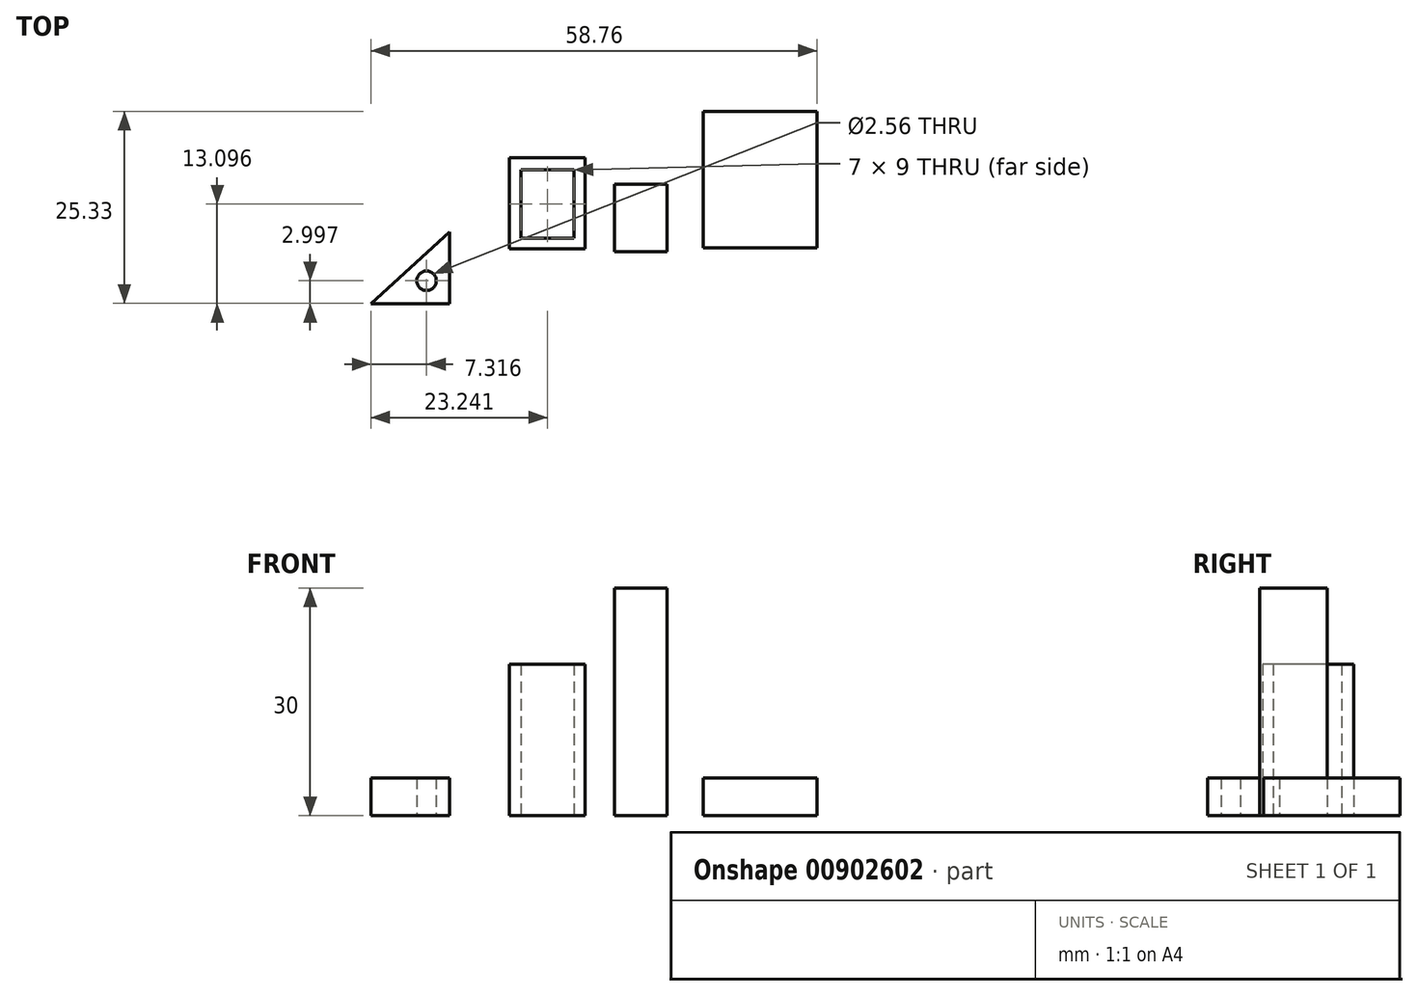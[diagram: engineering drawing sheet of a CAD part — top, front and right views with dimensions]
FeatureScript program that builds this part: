
annotation { "Feature Type Name" : "Feature", "Feature Type Description" : "" }
export const myFeature = defineFeature(function(context is Context, id is Id, definition is map)
    precondition{}
    {
        {
            var Q0;
            Q0=qCreatedBy(makeId("Top.planeOp"),FACE);
            var sketch = newSketch(context, id + "F0", { "sketchPlane" : qUnion([Q0])});
            skLineSegment(sketch, "E0", {"start": v(-29.03, -4.2) * mm, "end": v(-39.38, -13.62) * mm});
            skLineSegment(sketch, "E1", {"start": v(-39.38, -13.62) * mm, "end": v(-29.03, -13.62) * mm});
            skLineSegment(sketch, "E2", {"start": v(-29.03, -4.2) * mm, "end": v(-29.03, -13.62) * mm});
            skPoint(sketch, "E3.center.orphan", {"position": v(-11.7, -10.62) * mm});
            skPoint(sketch, "E4.start.orphan", {"position": v(-14.59, -4.2) * mm});
            skPoint(sketch, "E5.end.orphan", {"position": v(-14.59, -13.62) * mm});
            skPoint(sketch, "E5.start.orphan", {"position": v(-4.24, -13.62) * mm});
            skPoint(sketch, "E6.center.orphan", {"position": v(-32.06, -10.62) * mm});
            skCircle(sketch, "E7", {"center": v(-32.06, -10.62) * mm, "radius": 1.28 * mm});
            skSolve(sketch);
        }
        {
            var Q0;
            Q0=qCreatedBy(makeId("Top.planeOp"),FACE);
            var sketch = newSketch(context, id + "F1", { "sketchPlane" : qUnion([Q0])});
            skLineSegment(sketch, "E8.bottom", {"start": v(-21.17, 5.6) * mm, "end": v(-11.17, 5.6) * mm});
            skLineSegment(sketch, "E8.top", {"start": v(-21.17, -6.4) * mm, "end": v(-11.17, -6.4) * mm});
            skLineSegment(sketch, "E8.left", {"start": v(-21.17, 5.6) * mm, "end": v(-21.17, -6.4) * mm});
            skLineSegment(sketch, "E8.right", {"start": v(-11.17, 5.6) * mm, "end": v(-11.17, -6.4) * mm});
            skLineSegment(sketch, "E9.bottom", {"start": v(-19.64, 3.98) * mm, "end": v(-12.64, 3.98) * mm});
            skLineSegment(sketch, "E9.top", {"start": v(-19.64, -5.02) * mm, "end": v(-12.64, -5.02) * mm});
            skLineSegment(sketch, "E9.left", {"start": v(-19.64, 3.98) * mm, "end": v(-19.64, -5.02) * mm});
            skLineSegment(sketch, "E9.right", {"start": v(-12.64, 3.98) * mm, "end": v(-12.64, -5.02) * mm});
            skSolve(sketch);
        }
        {
            var Q0;
            Q0=qCreatedBy(makeId("Top.planeOp"),FACE);
            var sketch = newSketch(context, id + "F2", { "sketchPlane" : qUnion([Q0])});
            skLineSegment(sketch, "E10.bottom", {"start": v(-7.3, 2.09) * mm, "end": v(-0.4, 2.09) * mm});
            skLineSegment(sketch, "E10.top", {"start": v(-7.3, -6.81) * mm, "end": v(-0.4, -6.81) * mm});
            skLineSegment(sketch, "E10.left", {"start": v(-7.3, 2.09) * mm, "end": v(-7.3, -6.81) * mm});
            skLineSegment(sketch, "E10.right", {"start": v(-0.4, 2.09) * mm, "end": v(-0.4, -6.81) * mm});
            skSolve(sketch);
        }
        {
            var Q0;
            Q0=makeQuery(id+"F0.imprint","IMPRINT",FACE,{"disambiguationData":[TD([[makeQuery(id+"F0.imprint","IMPRINT",EDGE,{"derivedFrom":sQuery(id+"F0.wireOp",EDGE,"E0")}),1.0]])]});
            extrude(context, id + "F3", {"entities" : qUnion([Q0]), "depth" : 5 * mm, "offsetDistance" : 25 * mm});
        }
        {
            var Q0;
            Q0=makeQuery(id+"F1.imprint","IMPRINT",FACE,{"disambiguationData":[TD([[makeQuery(id+"F1.imprint","IMPRINT",EDGE,{"derivedFrom":sQuery(id+"F1.wireOp",EDGE,"E8.bottom")}),-1.0]])]});
            extrude(context, id + "F4", {"entities" : qUnion([Q0]), "depth" : 20 * mm, "offsetDistance" : 25 * mm});
        }
        {
            var Q0;
            Q0=makeQuery(id+"F2.imprint","IMPRINT",FACE,{"disambiguationData":[TD([[makeQuery(id+"F2.imprint","IMPRINT",EDGE,{"derivedFrom":sQuery(id+"F2.wireOp",EDGE,"E10.bottom")}),-1.0]])]});
            extrude(context, id + "F5", {"entities" : qUnion([Q0]), "depth" : 30 * mm, "offsetDistance" : 25 * mm});
        }
        {
            var Q0;
            Q0=qCreatedBy(makeId("Top.planeOp"),FACE);
            var sketch = newSketch(context, id + "F6", { "sketchPlane" : qUnion([Q0])});
            skLineSegment(sketch, "E11.bottom", {"start": v(4.38, 11.71) * mm, "end": v(19.38, 11.71) * mm});
            skLineSegment(sketch, "E11.top", {"start": v(4.38, -6.29) * mm, "end": v(19.38, -6.29) * mm});
            skLineSegment(sketch, "E11.left", {"start": v(4.38, 11.71) * mm, "end": v(4.38, -6.29) * mm});
            skLineSegment(sketch, "E11.right", {"start": v(19.38, 11.71) * mm, "end": v(19.38, -6.29) * mm});
            skSolve(sketch);
        }
        {
            var Q0;
            Q0=makeQuery(id+"F6.imprint","IMPRINT",FACE,{"disambiguationData":[TD([[makeQuery(id+"F6.imprint","IMPRINT",EDGE,{"derivedFrom":sQuery(id+"F6.wireOp",EDGE,"E11.bottom")}),-1.0]])]});
            extrude(context, id + "F7", {"entities" : qUnion([Q0]), "depth" : 5 * mm, "offsetDistance" : 25 * mm});
        }
    });
